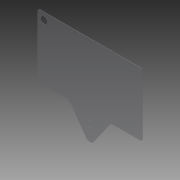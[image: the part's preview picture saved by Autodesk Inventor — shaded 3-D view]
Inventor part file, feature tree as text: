
AUTODESK INVENTOR PART (.ipt)
format: ipt  version: 2014 (Build 180170000, 170)  size: 139,776 bytes
history: native  units: in
note: dims shown in document units (in); Inventor stores cm internally (conversion verified against a paired STEP export)
features: extrude x2, sketch x2, fillet x1
ambient origin geometry x8: Origin, YZ Plane, XZ Plane, XY Plane, X Axis, Y Axis, Z Axis, Center Point
bodies: Solid1 (feature_tree)
feature tree (5):
  extrude  "Extrusion1"  Depth=17.0in
  fillet  "Fillet1"  Radius=17.0in
  extrude  "Extrusion2"  Depth=0.0625in
  sketch  "Sketch1"  dims[d0=1.0in d2=10.0in d3=17.0in]
  sketch  "Sketch2"  dims[d4=5.0in d5=6.0in d6=0.164in d7=0.5in d8=1.5748in d10=1.0in d11=0.3937in d13=1.0in d15=0.0625in d16=0.0in d17=0.5in d18=1.25in d19=1.375in d20=1.25in d21=4.3307in d23=1.75in d24=3.1496in d26=1.75in d29=0.0625in d30=0.0in]
